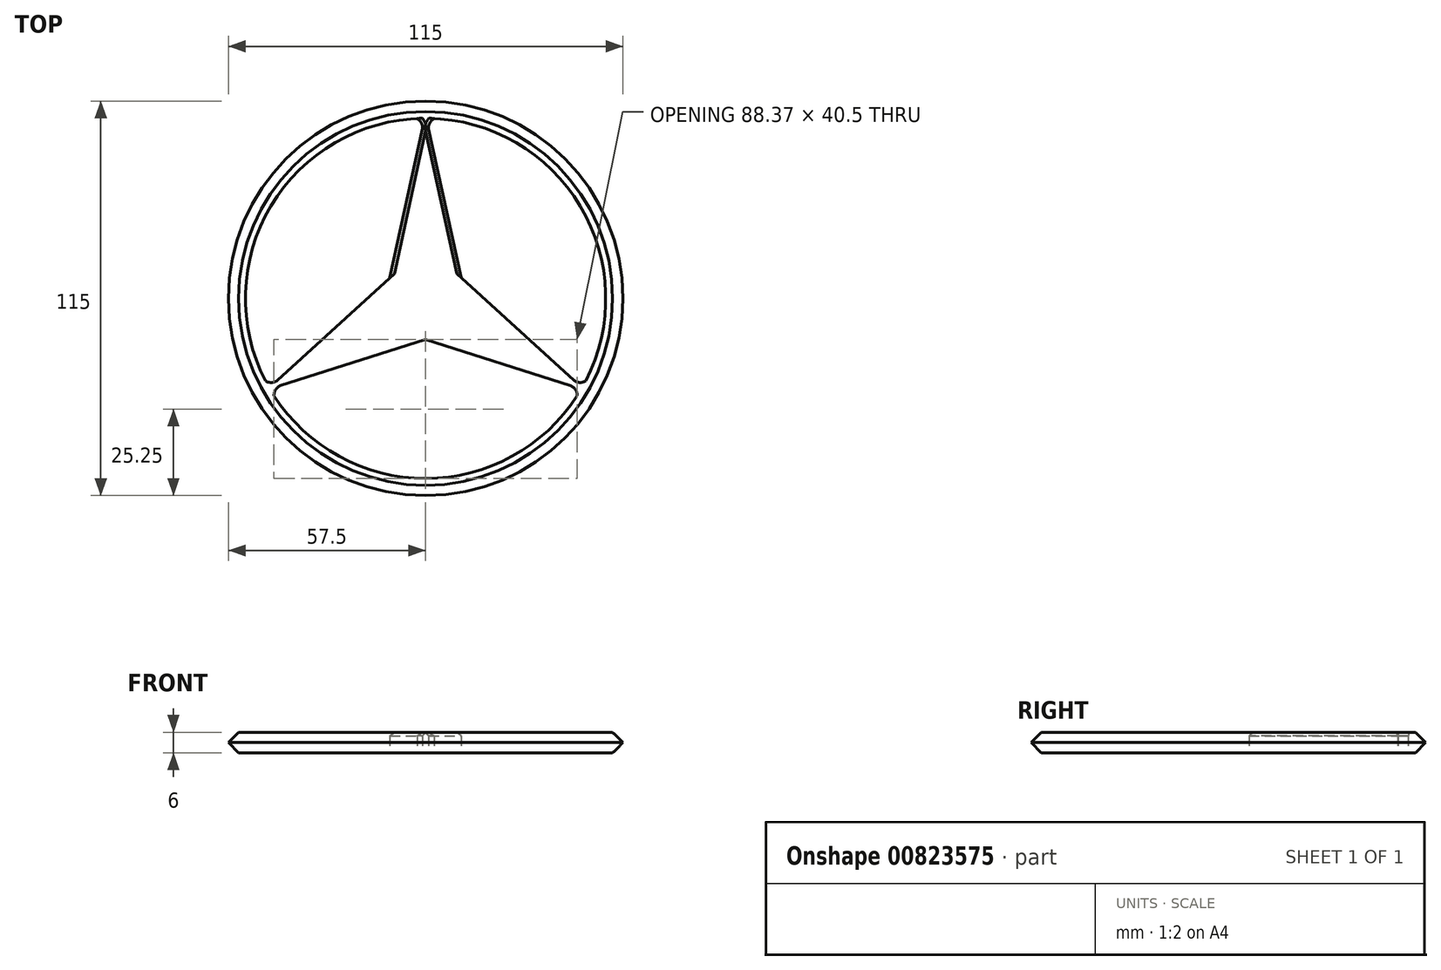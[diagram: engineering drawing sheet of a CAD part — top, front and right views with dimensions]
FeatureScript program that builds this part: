
annotation { "Feature Type Name" : "Feature", "Feature Type Description" : "" }
export const myFeature = defineFeature(function(context is Context, id is Id, definition is map)
    precondition{}
    {
        {
            var Q0;
            Q0=qCreatedBy(makeId("Top.planeOp"),FACE);
            var sketch = newSketch(context, id + "F0", { "sketchPlane" : qUnion([Q0])});
            skCircle(sketch, "E0", {"center": v(0, 0) * mm, "radius": 52.5 * mm});
            skLineSegment(sketch, "E1", {"start": v(0, 0) * mm, "end": v(0, 52.5) * mm});
            skLineSegment(sketch, "E2.1.0", {"start": v(0, 0) * mm, "end": v(-45.47, -26.25) * mm});
            skLineSegment(sketch, "E2.2.0", {"start": v(0, 0) * mm, "end": v(45.47, -26.25) * mm});
            skLineSegment(sketch, "E3", {"start": v(0, 0) * mm, "end": v(0, -12) * mm});
            skLineSegment(sketch, "E4.1.0", {"start": v(0, 0) * mm, "end": v(10.4, 6) * mm});
            skLineSegment(sketch, "E4.2.0", {"start": v(0, 0) * mm, "end": v(-10.4, 6) * mm});
            skLineSegment(sketch, "E5", {"start": v(0, -12) * mm, "end": v(-42.42, -25.5) * mm});
            skLineSegment(sketch, "E6.1.0", {"start": v(10.4, 6) * mm, "end": v(43.3, -23.98) * mm});
            skLineSegment(sketch, "E6.2.0", {"start": v(-10.4, 6) * mm, "end": v(-0.88, 49.5) * mm});
            skLineSegment(sketch, "E7", {"start": v(-10.4, 6) * mm, "end": v(-43.17, -23.89) * mm});
            skLineSegment(sketch, "E8.1.0", {"start": v(0, -12) * mm, "end": v(42.27, -25.44) * mm});
            skLineSegment(sketch, "E8.2.0", {"start": v(10.4, 6) * mm, "end": v(0.9, 49.33) * mm});
            skCircle(sketch, "E9", {"center": v(0, 0) * mm, "radius": 57.5 * mm});
            skArc(sketch, "E10", {"start": v(2.47, 52.44) * mm, "mid": v(1.2, 51.13) * mm, "end": v(0.9, 49.33) * mm});
            skArc(sketch, "E11.MirrorCS", {"start": v(-2.47, 52.44) * mm, "mid": v(-1.2, 51.13) * mm, "end": v(-0.9, 49.33) * mm});
            skArc(sketch, "E12.2.0", {"start": v(-46.65, -24.09) * mm, "mid": v(-44.88, -24.52) * mm, "end": v(-43.17, -23.89) * mm});
            skArc(sketch, "E12.2.1", {"start": v(-44.18, -28.36) * mm, "mid": v(-43.67, -26.6) * mm, "end": v(-42.27, -25.44) * mm});
            skArc(sketch, "E12.4.0", {"start": v(44.18, -28.36) * mm, "mid": v(43.67, -26.6) * mm, "end": v(42.27, -25.44) * mm});
            skArc(sketch, "E12.4.1", {"start": v(46.65, -24.09) * mm, "mid": v(44.88, -24.52) * mm, "end": v(43.17, -23.89) * mm});
            skPoint(sketch, "E13.orphan", {"position": v(45.58, -26.06) * mm});
            skPoint(sketch, "E14.orphan", {"position": v(45.36, -26.43) * mm});
            skPoint(sketch, "E15.orphan", {"position": v(-45.57, -26.07) * mm});
            skPoint(sketch, "E16.orphan", {"position": v(-45.35, -26.44) * mm});
            skPoint(sketch, "E17.orphan", {"position": v(-0.22, 52.5) * mm});
            skPoint(sketch, "E18.orphan", {"position": v(0.2, 52.5) * mm});
            skSolve(sketch);
        }
        {
            var Q0;
            Q0=makeQuery(id+"F0.imprint","IMPRINT",FACE,{"disambiguationData":[TD([[makeQuery(id+"F0.imprint","IMPRINT",EDGE,{"derivedFrom":sQuery(id+"F0.wireOp",EDGE,"5ZMQ3FgW-66mD-8fOE-FIj9-4Ftj0G2tJfpd")}),1.0]])]});
            var Q1;
            Q1=makeQuery(id+"F0.imprint","IMPRINT",FACE,{"disambiguationData":[TD([[makeQuery(id+"F0.imprint","IMPRINT",EDGE,{"derivedFrom":sQuery(id+"F0.wireOp",EDGE,"E9")}),1.0]])]});
            extrude(context, id + "F1", {"entities" : qUnion([Q0, Q1]), "depth" : 6 * mm, "offsetDistance" : 25 * mm});
        }
        {
            var Q0;
            Q0=makeQuery(id+"F1.opExtrude","CAP_EDGE",EDGE,{"disambiguationData":[OSD([sQuery(id+"F0.wireOp",EDGE,"E9")])],"isStart":false});
            var Q1;
            Q1=makeQuery(id+"F1.opExtrude","CAP_EDGE",EDGE,{"disambiguationData":[OSD([sQuery(id+"F0.wireOp",EDGE,"E9")])],"isStart":true});
            chamfer(context, id + "F2", {"entities" : qUnion([Q0, Q1]), "width" : 3 * mm, "tangentPropagation" : true});
        }
        {
            var Q0;
            {var subQ0=sQuery(id+"F0.wireOp",EDGE,"E1");Q0=makeQuery(id+"F0.imprint","IMPRINT",FACE,{"disambiguationData":[TD([[makeQuery(id+"F0.imprint","IMPRINT",EDGE,{"derivedFrom":subQ0}),-1.0]])]});}
            var Q1;
            {var subQ0=sQuery(id+"F0.wireOp",EDGE,"E2.2.0");Q1=makeQuery(id+"F0.imprint","IMPRINT",FACE,{"disambiguationData":[TD([[makeQuery(id+"F0.imprint","IMPRINT",EDGE,{"derivedFrom":subQ0}),1.0]])]});}
            var Q2;
            {var subQ0=sQuery(id+"F0.wireOp",EDGE,"E2.2.0");Q2=makeQuery(id+"F0.imprint","IMPRINT",FACE,{"disambiguationData":[TD([[makeQuery(id+"F0.imprint","IMPRINT",EDGE,{"derivedFrom":subQ0}),-1.0]])]});}
            var Q3;
            {var subQ0=sQuery(id+"F0.wireOp",EDGE,"E2.1.0");Q3=makeQuery(id+"F0.imprint","IMPRINT",FACE,{"disambiguationData":[TD([[makeQuery(id+"F0.imprint","IMPRINT",EDGE,{"derivedFrom":subQ0}),-1.0]])]});}
            var Q4;
            {var subQ0=sQuery(id+"F0.wireOp",EDGE,"E2.1.0");Q4=makeQuery(id+"F0.imprint","IMPRINT",FACE,{"disambiguationData":[TD([[makeQuery(id+"F0.imprint","IMPRINT",EDGE,{"derivedFrom":subQ0}),1.0]])]});}
            var Q5;
            {var subQ0=sQuery(id+"F0.wireOp",EDGE,"E1");Q5=makeQuery(id+"F0.imprint","IMPRINT",FACE,{"disambiguationData":[TD([[makeQuery(id+"F0.imprint","IMPRINT",EDGE,{"derivedFrom":subQ0}),1.0]])]});}
            extrude(context, id + "F3", {"entities" : qUnion([Q0, Q1, Q2, Q3, Q4, Q5]), "operationType" : NewBodyOperationType.ADD, "depth" : 6 * mm, "offsetDistance" : 25 * mm});
        }
        {
            var Q0;
            Q0=makeQuery(id+"F3.opExtrude","CAP_EDGE",EDGE,{"disambiguationData":[OSD([sQuery(id+"F0.wireOp",EDGE,"E8.2.0")])],"isStart":false});
            var Q1;
            Q1=makeQuery(id+"F3.opExtrude","CAP_EDGE",EDGE,{"disambiguationData":[OSD([sQuery(id+"F0.wireOp",EDGE,"E10")])],"isStart":false});
            var Q2;
            Q2=makeQuery(id+"F3.opExtrude","CAP_EDGE",EDGE,{"disambiguationData":[OSD([sQuery(id+"F0.wireOp",EDGE,"E6.2.0")])],"isStart":false});
            var Q3;
            Q3=makeQuery(id+"F3.opExtrude","CAP_EDGE",EDGE,{"disambiguationData":[OSD([sQuery(id+"F0.wireOp",EDGE,"E11.MirrorCS")])],"isStart":false});
            chamfer(context, id + "F4", {"entities" : qUnion([Q0, Q1, Q2, Q3]), "width" : 1 * mm, "tangentPropagation" : true});
        }
    });
